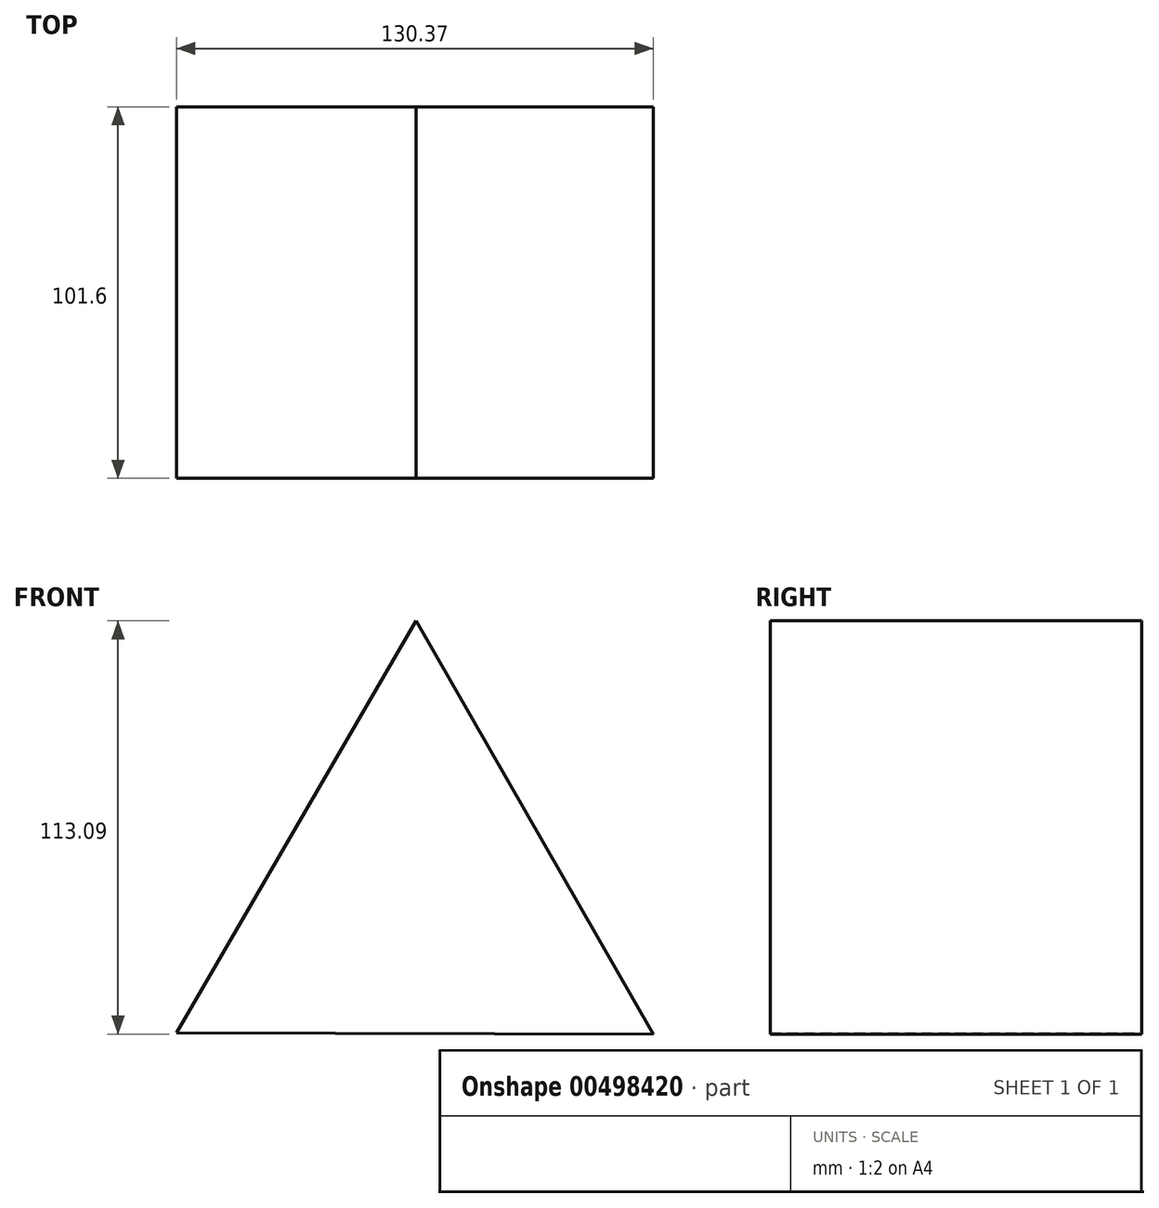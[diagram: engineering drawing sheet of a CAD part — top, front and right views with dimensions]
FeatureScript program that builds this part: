
annotation { "Feature Type Name" : "Feature", "Feature Type Description" : "" }
export const myFeature = defineFeature(function(context is Context, id is Id, definition is map)
    precondition{}
    {
        {
            var Q0;
            Q0=qCreatedBy(makeId("Front.planeOp"),FACE);
            var sketch = newSketch(context, id + "F0", { "sketchPlane" : qUnion([Q0])});
            skCircle(sketch, "E0.cCircle", {"center": v(0, 0) * mm, "radius": 75.27 * mm, "construction": true});
            skLineSegment(sketch, "E0.0", {"start": v(0.2, 75.27) * mm, "end": v(65.08, -37.82) * mm});
            skLineSegment(sketch, "E0.1", {"start": v(65.08, -37.82) * mm, "end": v(-65.3, -37.45) * mm});
            skLineSegment(sketch, "E0.2", {"start": v(-65.3, -37.45) * mm, "end": v(0.2, 75.27) * mm});
            skSolve(sketch);
        }
        {
            var Q0;
            Q0=makeQuery(id+"F0.imprint","IMPRINT",FACE,{"disambiguationData":[TD([[makeQuery(id+"F0.imprint","IMPRINT",EDGE,{"derivedFrom":sQuery(id+"F0.wireOp",EDGE,"E0.0")}),-1.0]])]});
            extrude(context, id + "F1", {"entities" : qUnion([Q0]), "depth" : 101.6 * mm, "symmetric" : true});
        }
    });
